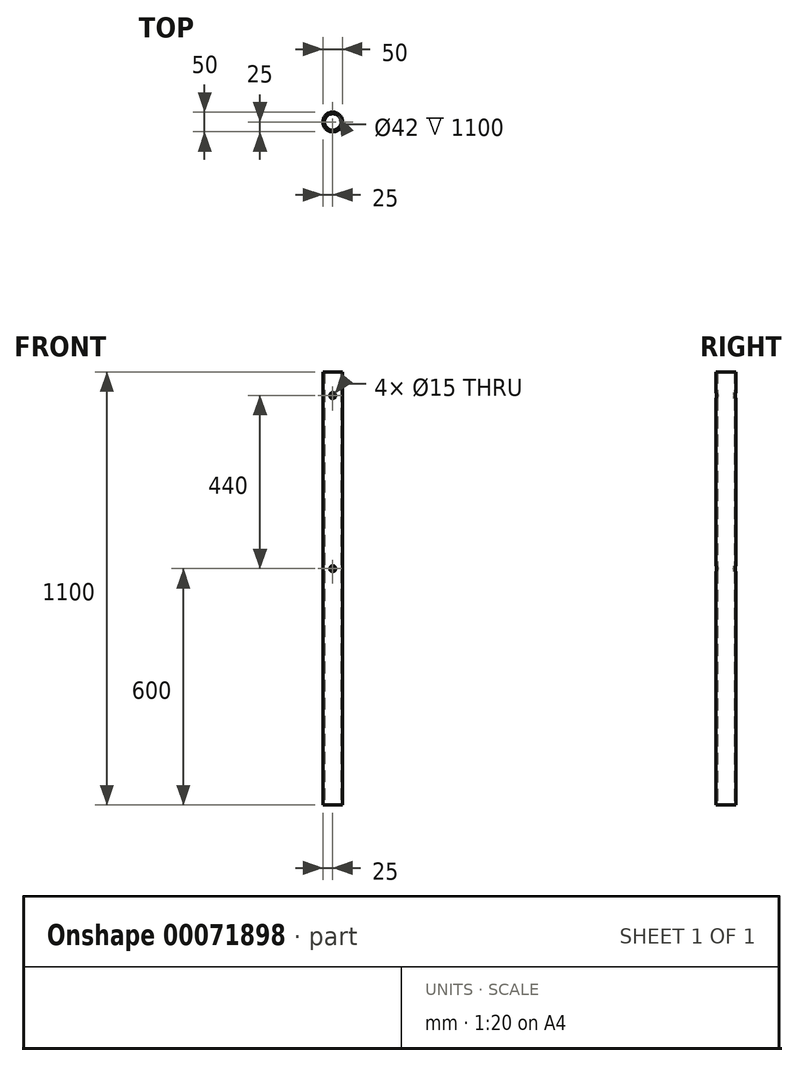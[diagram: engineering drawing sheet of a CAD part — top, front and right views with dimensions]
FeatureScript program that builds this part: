
annotation { "Feature Type Name" : "Feature", "Feature Type Description" : "" }
export const myFeature = defineFeature(function(context is Context, id is Id, definition is map)
    precondition{}
    {
        {
            var Q0;
            Q0=qCreatedBy(makeId("Top.planeOp"),FACE);
            var sketch = newSketch(context, id + "F0", { "sketchPlane" : qUnion([Q0])});
            skPoint(sketch, "E0.middle", {"position": v(0, 0) * mm});
            skCircle(sketch, "E1", {"center": v(0, 0) * mm, "radius": 25 * mm});
            skCircle(sketch, "E2", {"center": v(0, 0) * mm, "radius": 21 * mm});
            skSolve(sketch);
        }
        {
            var Q0;
            Q0 = qSketchRegion(id + "F0", true);
            extrude(context, id + "F1", {"entities" : qUnion([Q0]), "depth" : 1100 * mm});
        }
        {
            var Q0;
            Q0=qCreatedBy(makeId("Front.planeOp"),FACE);
            var sketch = newSketch(context, id + "F2", { "sketchPlane" : qUnion([Q0])});
            skCircle(sketch, "E3", {"center": v(0, 600) * mm, "radius": 7.5 * mm});
            skCircle(sketch, "E4", {"center": v(0, 1040) * mm, "radius": 7.5 * mm});
            skSolve(sketch);
        }
        {
            var Q0;
            Q0 = qSketchRegion(id + "F2", true);
            extrude(context, id + "F3", {"entities" : qUnion([Q0]), "operationType" : NewBodyOperationType.REMOVE, "endBound" : BoundingType.THROUGH_ALL, "oppositeDirection" : true, "depth" : 25 * mm, "hasSecondDirection" : true, "secondDirectionBound" : SecondDirectionBoundingType.THROUGH_ALL, "secondDirectionOppositeDirection" : false, "secondDirectionDepth" : 25 * mm});
        }
    });
